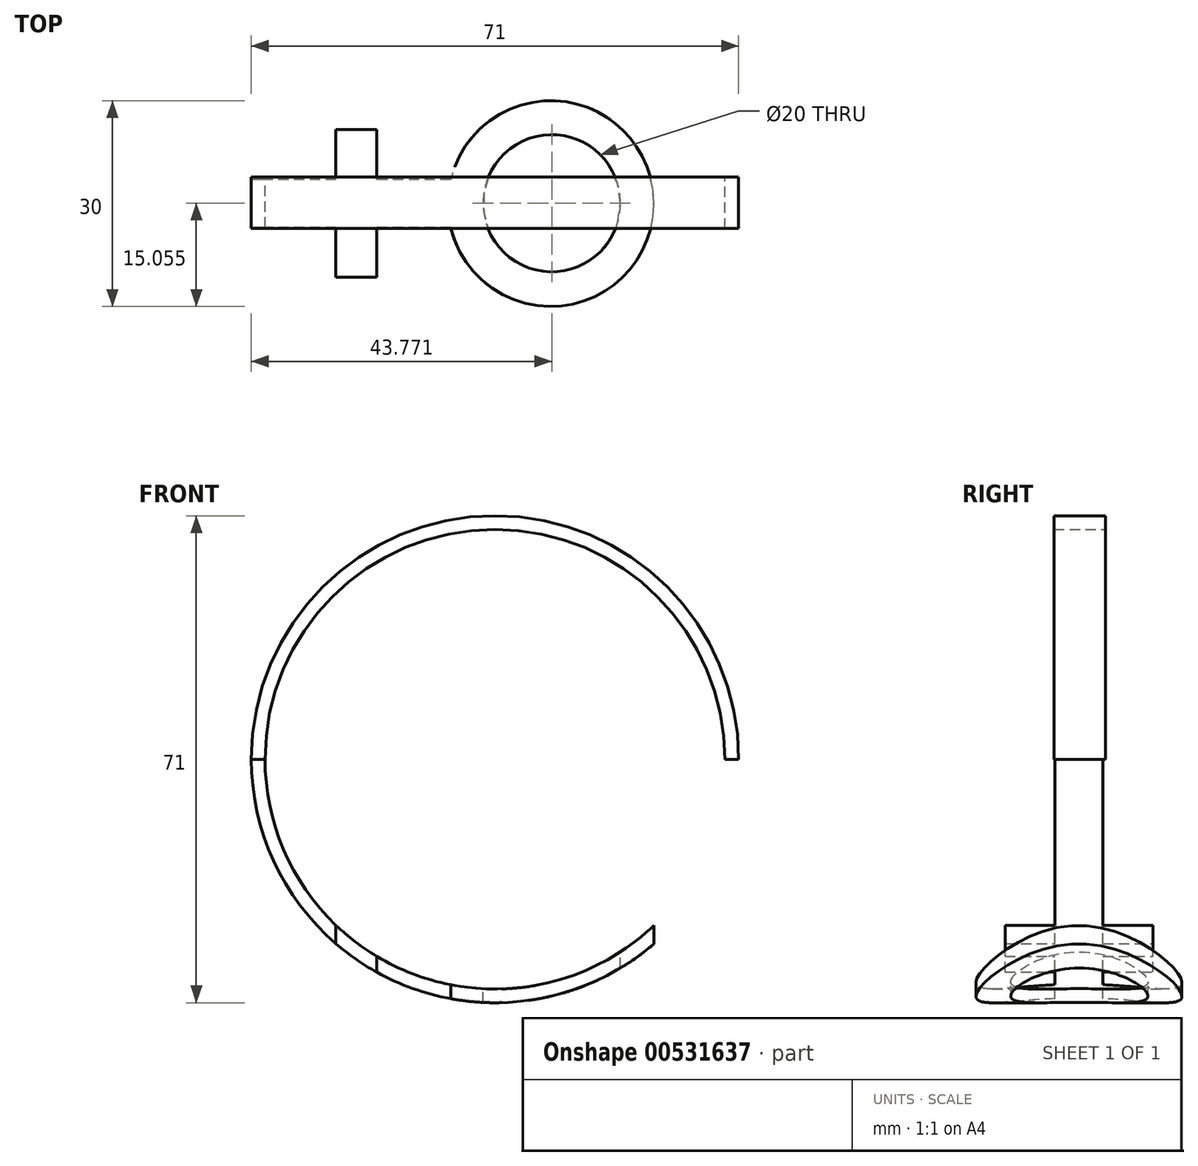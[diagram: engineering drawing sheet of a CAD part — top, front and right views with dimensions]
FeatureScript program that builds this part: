
annotation { "Feature Type Name" : "Feature", "Feature Type Description" : "" }
export const myFeature = defineFeature(function(context is Context, id is Id, definition is map)
    precondition{}
    {
        {
            var Q0;
            Q0=qCreatedBy(makeId("Front.planeOp"),FACE);
            var sketch = newSketch(context, id + "F0", { "sketchPlane" : qUnion([Q0])});
            skCircle(sketch, "E0", {"center": v(0, 0) * mm, "radius": 33.5 * mm});
            skCircle(sketch, "E1", {"center": v(0, 0) * mm, "radius": 35.5 * mm});
            skSolve(sketch);
        }
        {
            var Q0;
            Q0=makeQuery(id+"F0.imprint","IMPRINT",FACE,{"disambiguationData":[TD([[makeQuery(id+"F0.imprint","IMPRINT",EDGE,{"derivedFrom":sQuery(id+"F0.wireOp",EDGE,"E0")}),-1.0]])]});
            extrude(context, id + "F1", {"entities" : qUnion([Q0]), "depth" : 50.8 * mm, "offsetDistance" : 25.4 * mm});
        }
        {
            var Q0;
            Q0=qCreatedBy(makeId("Top.planeOp"),FACE);
            var sketch = newSketch(context, id + "F2", { "sketchPlane" : qUnion([Q0])});
            skCircle(sketch, "E2", {"center": v(8.13, -25.79) * mm, "radius": 12 * mm});
            skArc(sketch, "E3", {"start": v(-6.46, -29.29) * mm, "mid": v(23.13, -25.79) * mm, "end": v(-6.46, -22.29) * mm});
            skLineSegment(sketch, "E4", {"start": v(-6.46, -22.29) * mm, "end": v(-13.5, -22.29) * mm});
            skLineSegment(sketch, "E5", {"start": v(-6.87, -25.79) * mm, "end": v(-13.18, -25.79) * mm});
            skLineSegment(sketch, "E6.MirrorCS", {"start": v(-6.46, -29.29) * mm, "end": v(-13.5, -29.29) * mm});
            skLineSegment(sketch, "E7", {"start": v(-10.81, -22.29) * mm, "end": v(-17.23, -22.29) * mm});
            skLineSegment(sketch, "E8", {"start": v(-13.5, -29.29) * mm, "end": v(-17.23, -29.29) * mm});
            skLineSegment(sketch, "E9", {"start": v(-37.1, -22.29) * mm, "end": v(-37.3, -29.29) * mm});
            skLineSegment(sketch, "E10", {"start": v(-17.23, -22.29) * mm, "end": v(-17.23, -15.02) * mm});
            skLineSegment(sketch, "E11", {"start": v(-17.23, -15.02) * mm, "end": v(-23.17, -15.02) * mm});
            skLineSegment(sketch, "E12", {"start": v(-23.17, -15.02) * mm, "end": v(-23.17, -22.29) * mm});
            skLineSegment(sketch, "E13.MirrorCS", {"start": v(-17.23, -36.55) * mm, "end": v(-23.17, -36.55) * mm});
            skLineSegment(sketch, "E14.MirrorCS", {"start": v(-17.23, -29.29) * mm, "end": v(-17.23, -36.55) * mm});
            skLineSegment(sketch, "E15.MirrorCS", {"start": v(-23.17, -36.55) * mm, "end": v(-23.17, -29.29) * mm});
            skLineSegment(sketch, "E16.trimOffspring", {"start": v(-23.17, -22.29) * mm, "end": v(-37.1, -22.29) * mm});
            skLineSegment(sketch, "E17.trimOffspring", {"start": v(-23.17, -29.29) * mm, "end": v(-37.3, -29.29) * mm});
            skLineSegment(sketch, "E18", {"start": v(-37.3, -29.29) * mm, "end": v(-37.3, -59.55) * mm});
            skLineSegment(sketch, "E19", {"start": v(-37.3, -59.55) * mm, "end": v(42.62, -59.55) * mm});
            skLineSegment(sketch, "E20", {"start": v(42.62, -59.55) * mm, "end": v(42.62, 5.55) * mm});
            skLineSegment(sketch, "E21", {"start": v(42.62, 5.55) * mm, "end": v(-37.3, 5.55) * mm});
            skLineSegment(sketch, "E22", {"start": v(-37.3, 5.55) * mm, "end": v(-37.1, -22.29) * mm});
            skSolve(sketch);
        }
        {
            var Q0;
            Q0=makeQuery(id+"F2.imprint","IMPRINT",FACE,{"disambiguationData":[TD([[makeQuery(id+"F2.imprint","IMPRINT",EDGE,{"derivedFrom":sQuery(id+"F2.wireOp",EDGE,"E3")}),-1.0]])]});
            extrude(context, id + "F3", {"entities" : qUnion([Q0]), "operationType" : NewBodyOperationType.REMOVE, "oppositeDirection" : true, "depth" : 50.8 * mm, "offsetDistance" : 25.4 * mm});
        }
        {
            var Q0;
            Q0=qCreatedBy(makeId("Top.planeOp"),FACE);
            var sketch = newSketch(context, id + "F4", { "sketchPlane" : qUnion([Q0])});
            skCircle(sketch, "E23", {"center": v(8.27, -25.74) * mm, "radius": 10 * mm});
            skSolve(sketch);
        }
        {
            var Q0;
            Q0=makeQuery(id+"F4.imprint","IMPRINT",FACE,{"disambiguationData":[TD([[makeQuery(id+"F4.imprint","IMPRINT",EDGE,{"derivedFrom":sQuery(id+"F4.wireOp",EDGE,"E23")}),1.0]])]});
            extrude(context, id + "F5", {"entities" : qUnion([Q0]), "operationType" : NewBodyOperationType.REMOVE, "oppositeDirection" : true, "depth" : 50.8 * mm, "offsetDistance" : 25.4 * mm});
        }
        {
            var Q0;
            Q0=qCreatedBy(makeId("Right.planeOp"),FACE);
            var sketch = newSketch(context, id + "F6", { "sketchPlane" : qUnion([Q0])});
            skLineSegment(sketch, "E24", {"start": v(-21.94, 0) * mm, "end": v(-21.94, 38.11) * mm});
            skLineSegment(sketch, "E25", {"start": v(-29.43, 0) * mm, "end": v(-29.43, 39.16) * mm});
            skLineSegment(sketch, "E26", {"start": v(-29.43, 39.16) * mm, "end": v(-21.94, 38.11) * mm});
            skLineSegment(sketch, "E27", {"start": v(-29.43, 39.16) * mm, "end": v(-57.44, 38.11) * mm});
            skLineSegment(sketch, "E28", {"start": v(-57.44, 38.11) * mm, "end": v(-57.44, 0) * mm});
            skLineSegment(sketch, "E29", {"start": v(-57.44, 0) * mm, "end": v(-29.43, 0) * mm});
            skLineSegment(sketch, "E30", {"start": v(-21.94, 38.11) * mm, "end": v(6.51, 37.07) * mm});
            skLineSegment(sketch, "E31", {"start": v(6.51, 37.07) * mm, "end": v(6.51, -3.37) * mm});
            skLineSegment(sketch, "E32", {"start": v(6.51, -3.37) * mm, "end": v(-21.94, -4.42) * mm});
            skLineSegment(sketch, "E33", {"start": v(-21.94, -4.42) * mm, "end": v(-21.94, 0) * mm});
            skSolve(sketch);
        }
        {
            var Q0;
            Q0=makeQuery(id+"F6.imprint","IMPRINT",FACE,{"disambiguationData":[TD([[makeQuery(id+"F6.imprint","IMPRINT",EDGE,{"derivedFrom":sQuery(id+"F6.wireOp",EDGE,"E24")}),-1.0]])]});
            var Q1;
            Q1=makeQuery(id+"F6.imprint","IMPRINT",FACE,{"disambiguationData":[TD([[makeQuery(id+"F6.imprint","IMPRINT",EDGE,{"derivedFrom":sQuery(id+"F6.wireOp",EDGE,"E25")}),1.0]])]});
            extrude(context, id + "F7", {"entities" : qUnion([Q0, Q1]), "operationType" : NewBodyOperationType.REMOVE, "endBound" : BoundingType.SYMMETRIC, "oppositeDirection" : true, "depth" : 76.2 * mm, "offsetDistance" : 25.4 * mm});
        }
    });
